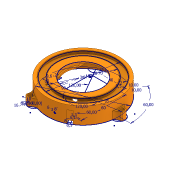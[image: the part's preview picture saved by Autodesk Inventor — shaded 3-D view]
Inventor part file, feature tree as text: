
AUTODESK INVENTOR PART (.ipt)
format: ipt  version: 2020.3 (Build 243373000, 373)  size: 338,944 bytes
history: native  units: mm
features: extrude x10, sketch x9, plane x3, revolve x1
ambient origin geometry x8: Origin, YZ Plane, XZ Plane, XY Plane, X Axis, Y Axis, Z Axis, Center Point
bodies: Body1 (feature_tree)
feature tree (23):
  sketch  "Sketch1"  dims[d0=95.0mm d1=120.0deg]
  plane  "Work Plane1"
  plane  "Work Plane2"
  plane  "Work Plane3"
  sketch  "Sketch2"  dims[d2=120.0deg d3=16.0mm]
  sketch  "Sketch3"  dims[d4=3.0mm d5=6.0mm]
  sketch  "Sketch4"  dims[d6=1.0mm d7=10.0mm]
  extrude  "Extrusion9"  TaperAngle=120.0deg  [1 undecoded]
  extrude  "Extrusion10"  Depth=16.0mm
  extrude  "Extrusion11"  Depth=6.0mm
  extrude  "Extrusion12"  Depth=10.0mm
  extrude  "Extrusion13"  Depth=2.4mm
  extrude  "Extrusion14"  Depth=30.0mm TaperAngle=360.0deg
  sketch  "Sketch5"  dims[d8=3.6mm d9=2.4mm]
  sketch  "Sketch6"  dims[d10=1.2mm d13=30.0mm d15=360.0deg]
  revolve  "Revolution1"  [1 undecoded]
  extrude  "Extrusion15"  Depth=6.0mm
  extrude  "Extrusion16"  TaperAngle=60.0deg  [1 undecoded]
  extrude  "Extrusion17"  Depth=6.1mm
  extrude  "Extrusion18"  Depth=8.0mm
  sketch  "Sketch7"  dims[d17=9.6mm d18=12.0mm]
  sketch  "Sketch8"  dims[d19=2.0mm d20=6.0mm]
  sketch  "Sketch9"  dims[d21=2.0mm d23=60.0deg d24=6.1mm d25=8.0mm d26=6.1mm d27=60.0deg d28=1.745329mm d29=1.745329mm d46=5.5mm d47=5.5mm d48=5.5mm d56=40.0mm d57=60.0mm d58=3.2mm d59=1.3mm d60=1.0mm d61=1.0mm d62=1.3mm d64=3.0mm d65=8.0mm d66=6.0mm d74=90.0mm d75=22.0mm d76=0.0mm d77=3.0mm d78=0.0mm d79=10.0mm d80=0.0mm d81=10.0mm d82=0.0mm d83=4.2mm d84=0.0mm d85=8.3mm d86=0.0mm d87=70.0mm d88=85.0mm d89=4.0mm d90=4.0mm d91=9.5mm d92=50.0mm d93=2.0mm d94=2.0mm d95=4.0mm d96=90.0deg d97=20.0mm d98=0.0mm d99=10.0mm d100=0.0mm d101=6.0mm d102=6.0mm d103=6.0mm d104=2.0mm d105=0.0mm d106=7.25mm d107=0.0mm d72=0.5mm d73=0.872665mm d108=0.5mm d109=0.872665mm]
note: 3 required parameter values undecoded (feature->parameter linkage not recoverable at this tier; creation-order binding heuristic only, values carry confidence <= 0.55)